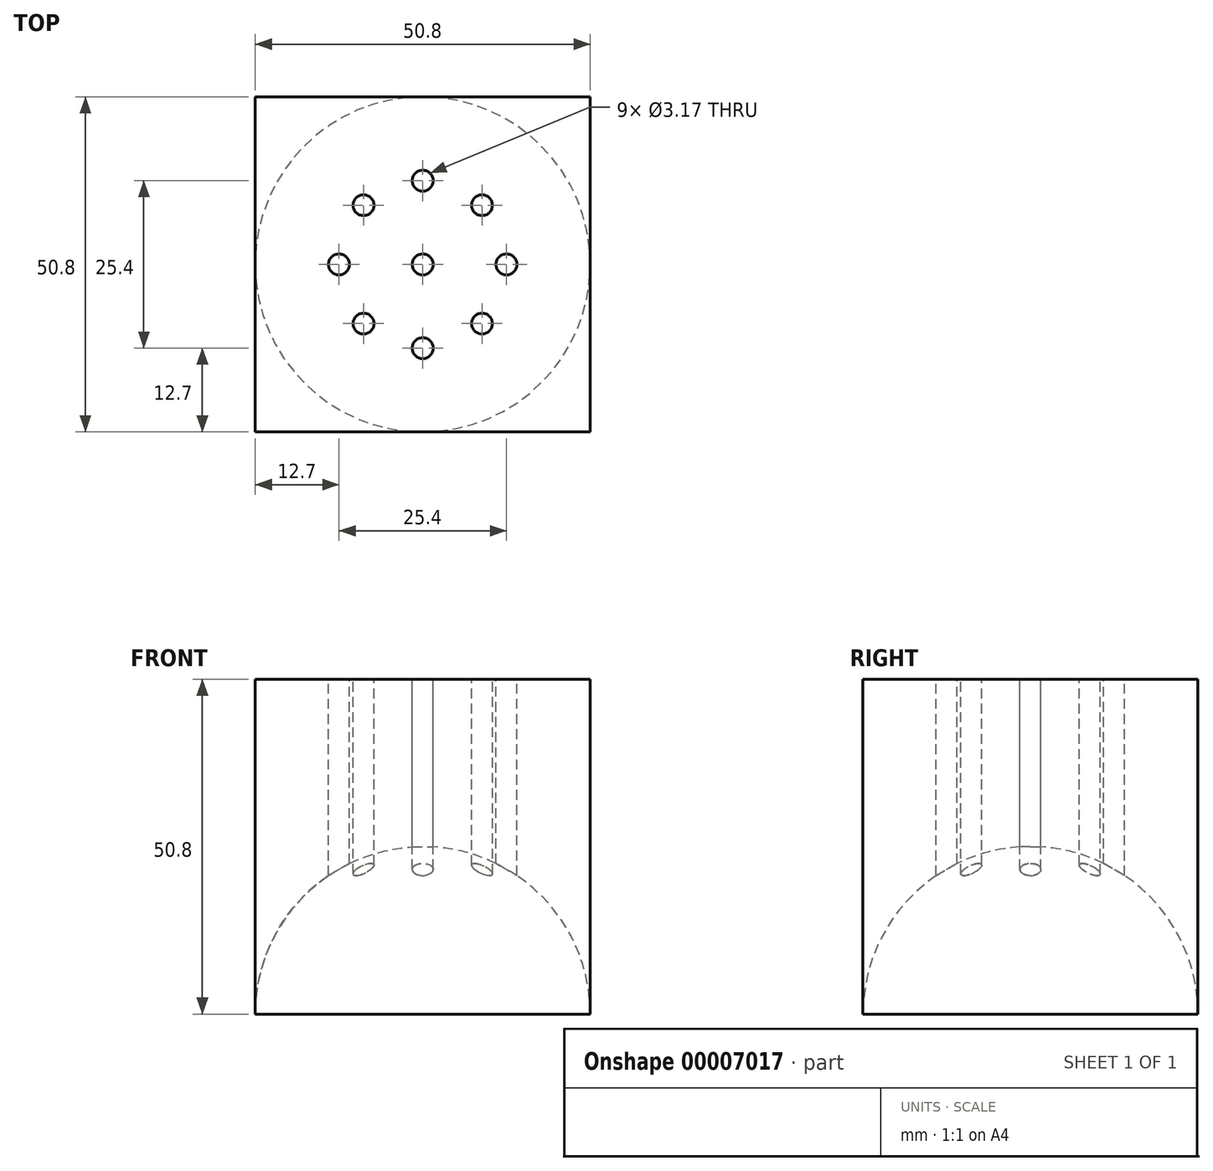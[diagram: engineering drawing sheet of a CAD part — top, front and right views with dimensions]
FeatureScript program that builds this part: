
annotation { "Feature Type Name" : "Feature", "Feature Type Description" : "" }
export const myFeature = defineFeature(function(context is Context, id is Id, definition is map)
    precondition{}
    {
        {
            var Q0;
            Q0=qCreatedBy(makeId("Right.planeOp"),FACE);
            var sketch = newSketch(context, id + "F0", { "sketchPlane" : qUnion([Q0])});
            skLineSegment(sketch, "E0.rect.bottom", {"start": v(-25.4, 25.4) * mm, "end": v(25.4, 25.4) * mm});
            skLineSegment(sketch, "E0.rect.top", {"start": v(-25.4, -25.4) * mm, "end": v(25.4, -25.4) * mm});
            skLineSegment(sketch, "E0.rect.left", {"start": v(-25.4, 25.4) * mm, "end": v(-25.4, -25.4) * mm});
            skLineSegment(sketch, "E0.rect.right", {"start": v(25.4, 25.4) * mm, "end": v(25.4, -25.4) * mm});
            skPoint(sketch, "E0.rect.middle", {"position": v(0, 0) * mm});
            skLineSegment(sketch, "E1", {"start": v(0, 0) * mm, "end": v(0, -25.4) * mm});
            skCircle(sketch, "E2", {"center": v(0, -25.4) * mm, "radius": 25.4 * mm});
            skSolve(sketch);
        }
        {
            var Q0;
            Q0=makeQuery(id+"F0.imprint","IMPRINT",FACE,{"disambiguationData":[TD([[makeQuery(id+"F0.imprint","IMPRINT",EDGE,{"derivedFrom":sQuery(id+"F0.wireOp",EDGE,"E0.rect.bottom")}),-1.0]])]});
            var Q1;
            {var subQ1=sQuery(id+"F0.wireOp",EDGE,"E1");Q1=makeQuery(id+"F0.imprint","IMPRINT",FACE,{"disambiguationData":[TD([[makeQuery(id+"F0.imprint","IMPRINT",EDGE,{"derivedFrom":subQ1}),-1.0]])]});}
            var Q2;
            {var subQ1=sQuery(id+"F0.wireOp",EDGE,"E1");Q2=makeQuery(id+"F0.imprint","IMPRINT",FACE,{"disambiguationData":[TD([[makeQuery(id+"F0.imprint","IMPRINT",EDGE,{"derivedFrom":subQ1}),1.0]])]});}
            extrude(context, id + "F1", {"entities" : qUnion([Q0, Q1, Q2]), "endBound" : BoundingType.SYMMETRIC, "depth" : 50.8 * mm});
        }
        {
            var Q0;
            {var subQ1=sQuery(id+"F0.wireOp",EDGE,"E0.rect.top");var subQ4=makeQuery(id+"F0.imprint","INTERSECT",VERTEX,{"derivedFrom":[subQ1,sQuery(id+"F0.wireOp",EDGE,"E1")]});Q0=makeQuery(id+"F0.imprint","IMPRINT",FACE,{"disambiguationData":[TD([[makeQuery(id+"F0.imprint","IMPRINT",EDGE,{"disambiguationData":[TD([[subQ4,1.0]])],"derivedFrom":subQ1}),-1.0]])]});}
            var sketch = newSketch(context, id + "F2", { "sketchPlane" : qUnion([Q0])});
            skArc(sketch, "E3", {"start": v(0, 0) * mm, "mid": v(-17.96, -7.44) * mm, "end": v(-25.4, -25.4) * mm});
            skLineSegment(sketch, "E4", {"start": v(0, -25.4) * mm, "end": v(0, 0) * mm});
            skLineSegment(sketch, "E5", {"start": v(0, -25.4) * mm, "end": v(-25.4, -25.4) * mm});
            skSolve(sketch);
        }
        {
            var Q0;
            Q0 = qSketchRegion(id + "F2", true);
            var Q1;
            Q1=sQuery(id+"F2.wireOp",EDGE,"E4");
            revolve(context, id + "F3", {"operationType" : NewBodyOperationType.REMOVE, "entities" : qUnion([Q0]), "axis" : qUnion([Q1]), "revolveType" : RevolveType.FULL, "oppositeDirection" : true});
        }
        {
            var Q0;
            Q0=makeQuery(id+"F1.opExtrude","SWEPT_FACE",FACE,{"disambiguationData":[OSD([sQuery(id+"F0.wireOp",EDGE,"E0.rect.bottom")])]});
            var sketch = newSketch(context, id + "F4", { "sketchPlane" : qUnion([Q0])});
            skCircle(sketch, "E6", {"center": v(0, 0) * mm, "radius": 1.59 * mm});
            skCircle(sketch, "E7", {"center": v(0, 12.7) * mm, "radius": 1.59 * mm});
            skCircle(sketch, "E8.1.0", {"center": v(-8.98, 8.98) * mm, "radius": 1.59 * mm});
            skCircle(sketch, "E8.2.0", {"center": v(-12.7, 0) * mm, "radius": 1.59 * mm});
            skCircle(sketch, "E8.3.0", {"center": v(-8.98, -8.98) * mm, "radius": 1.59 * mm});
            skCircle(sketch, "E8.4.0", {"center": v(0, -12.7) * mm, "radius": 1.59 * mm});
            skCircle(sketch, "E8.5.0", {"center": v(8.98, -8.98) * mm, "radius": 1.59 * mm});
            skCircle(sketch, "E8.6.0", {"center": v(12.7, 0) * mm, "radius": 1.59 * mm});
            skCircle(sketch, "E8.7.0", {"center": v(8.98, 8.98) * mm, "radius": 1.59 * mm});
            skSolve(sketch);
        }
        {
            var Q0;
            Q0 = qSketchRegion(id + "F4", true);
            extrude(context, id + "F5", {"entities" : qUnion([Q0]), "operationType" : NewBodyOperationType.REMOVE, "endBound" : BoundingType.THROUGH_ALL, "oppositeDirection" : true, "depth" : 25.4 * mm});
        }
    });
